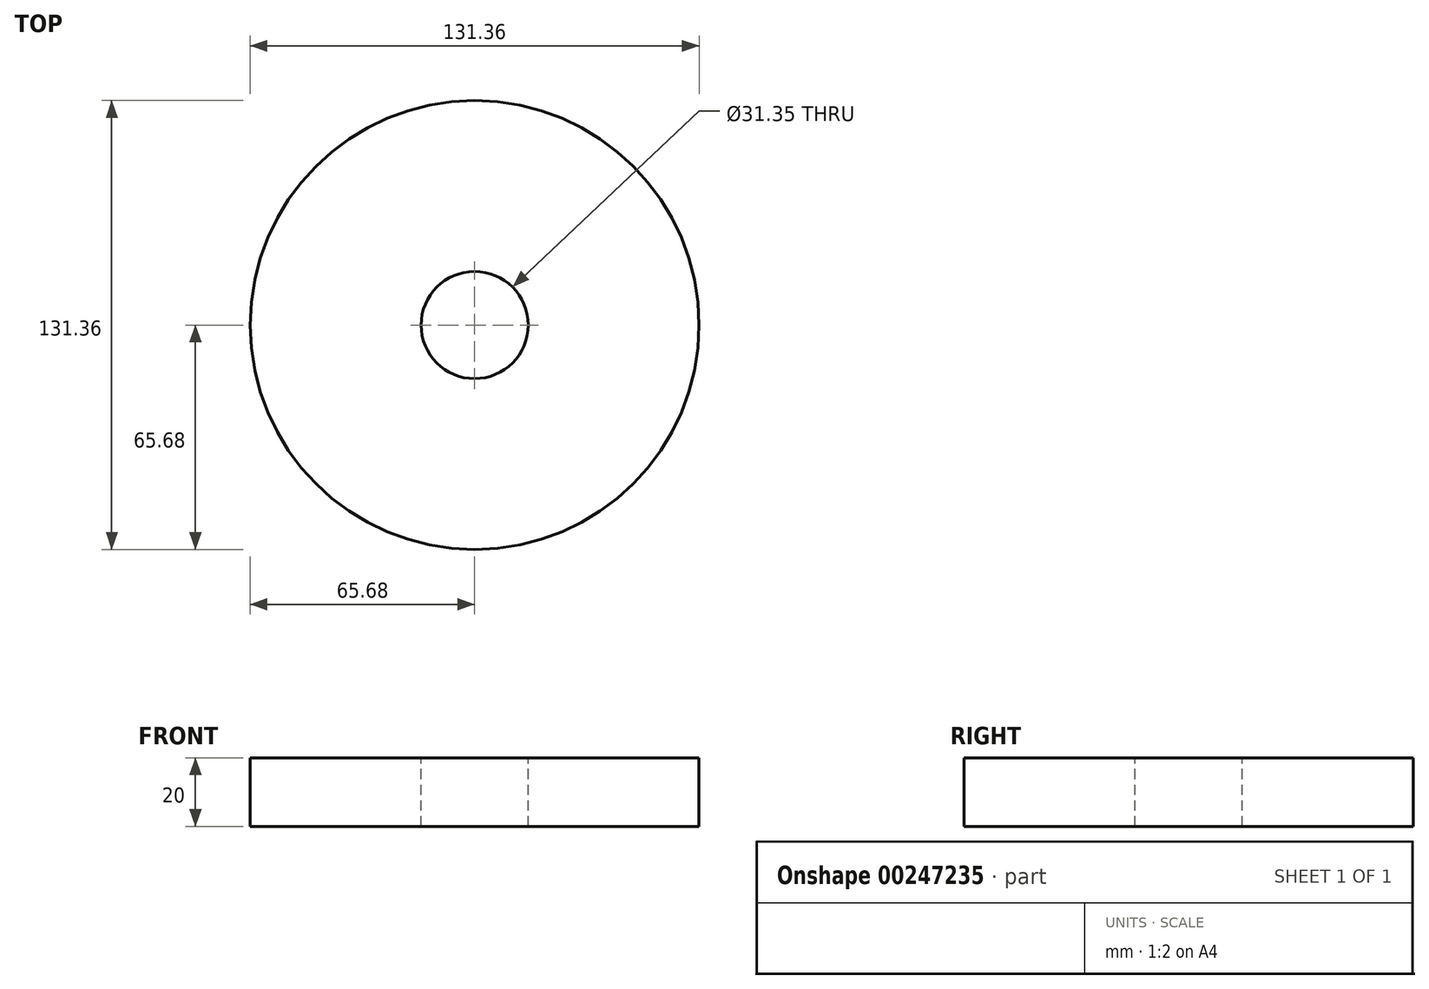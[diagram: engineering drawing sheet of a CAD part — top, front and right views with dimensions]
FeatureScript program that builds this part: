
annotation { "Feature Type Name" : "Feature", "Feature Type Description" : "" }
export const myFeature = defineFeature(function(context is Context, id is Id, definition is map)
    precondition{}
    {
        {
            var Q0;
            Q0=qCreatedBy(makeId("Front.planeOp"),FACE);
            var sketch = newSketch(context, id + "F0", { "sketchPlane" : qUnion([Q0])});
            skLineSegment(sketch, "E0", {"start": v(0, 71.82) * mm, "end": v(0, -74.53) * mm, "construction": true});
            skLineSegment(sketch, "E1.bottom", {"start": v(15.68, 10) * mm, "end": v(65.68, 10) * mm});
            skLineSegment(sketch, "E1.top", {"start": v(15.68, -10) * mm, "end": v(65.68, -10) * mm});
            skLineSegment(sketch, "E1.left", {"start": v(15.68, 10) * mm, "end": v(15.68, -10) * mm});
            skLineSegment(sketch, "E1.right", {"start": v(65.68, 10) * mm, "end": v(65.68, -10) * mm});
            skSolve(sketch);
        }
        {
            var Q0;
            Q0=makeQuery(id+"F0.imprint","IMPRINT",FACE,{"disambiguationData":[TD([[makeQuery(id+"F0.imprint","IMPRINT",EDGE,{"derivedFrom":sQuery(id+"F0.wireOp",EDGE,"E1.bottom")}),-1.0]])]});
            var Q1;
            Q1=sQuery(id+"F0.wireOp",EDGE,"E0");
            revolve(context, id + "F1", {"entities" : qUnion([Q0]), "axis" : qUnion([Q1]), "revolveType" : RevolveType.FULL});
        }
    });
